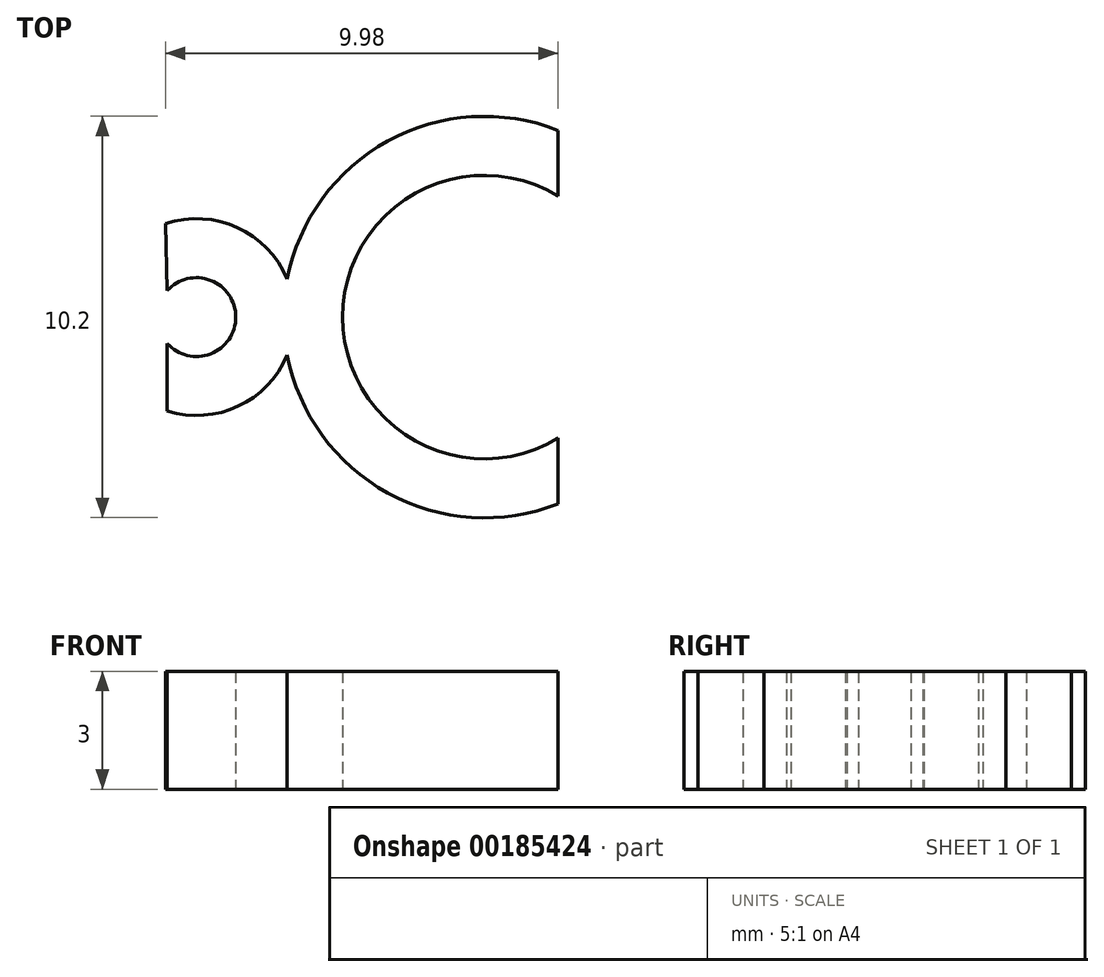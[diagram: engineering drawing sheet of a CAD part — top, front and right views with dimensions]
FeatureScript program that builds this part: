
annotation { "Feature Type Name" : "Feature", "Feature Type Description" : "" }
export const myFeature = defineFeature(function(context is Context, id is Id, definition is map)
    precondition{}
    {
        {
            var Q0;
            Q0=qCreatedBy(makeId("Top.planeOp"),FACE);
            var sketch = newSketch(context, id + "F0", { "sketchPlane" : qUnion([Q0])});
            skArc(sketch, "E0", {"start": v(3.18, 4.45) * mm, "mid": v(-2.3, 1.38) * mm, "end": v(3.18, -1.7) * mm});
            skArc(sketch, "E1", {"start": v(3.18, 6.12) * mm, "mid": v(-1.15, 5.85) * mm, "end": v(-3.7, 2.34) * mm});
            skLineSegment(sketch, "E2", {"start": v(3.18, -1.7) * mm, "end": v(3.18, -3.37) * mm});
            skLineSegment(sketch, "E3", {"start": v(3.18, 4.45) * mm, "end": v(3.18, 6.12) * mm});
            skArc(sketch, "E4", {"start": v(-6.75, 0.7) * mm, "mid": v(-5.01, 1.38) * mm, "end": v(-6.75, 2.05) * mm});
            skArc(sketch, "E5", {"start": v(-6.75, -1.01) * mm, "mid": v(-4.95, -0.89) * mm, "end": v(-3.7, 0.41) * mm});
            skLineSegment(sketch, "E6", {"start": v(-6.75, 2.05) * mm, "end": v(-6.8, 3.75) * mm});
            skLineSegment(sketch, "E7", {"start": v(-6.75, 0.7) * mm, "end": v(-6.75, -1.01) * mm});
            skArc(sketch, "E8.trimOffspring", {"start": v(-3.7, 0.41) * mm, "mid": v(-1.15, -3.1) * mm, "end": v(3.18, -3.37) * mm});
            skArc(sketch, "E9.trimOffspring", {"start": v(-3.7, 2.34) * mm, "mid": v(-4.97, 3.65) * mm, "end": v(-6.8, 3.75) * mm});
            skSolve(sketch);
        }
        {
            var Q0;
            Q0=makeQuery(id+"F0.imprint","IMPRINT",FACE,{"disambiguationData":[TD([[makeQuery(id+"F0.imprint","IMPRINT",EDGE,{"derivedFrom":sQuery(id+"F0.wireOp",EDGE,"E0")}),-1.0]])]});
            extrude(context, id + "F1", {"entities" : qUnion([Q0]), "depth" : 3 * mm});
        }
    });
